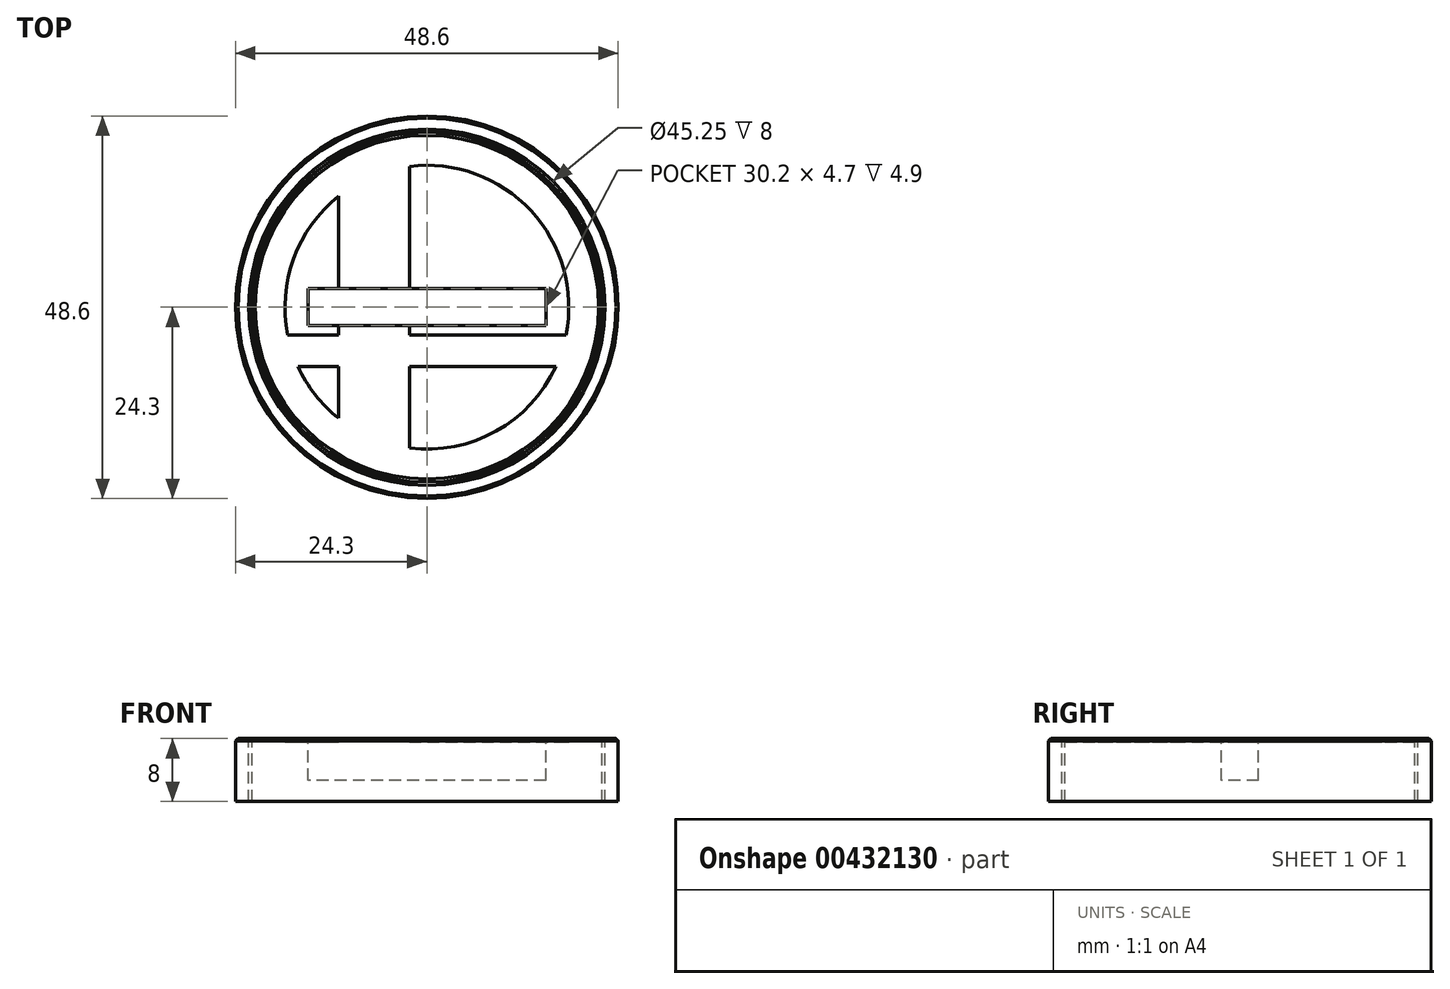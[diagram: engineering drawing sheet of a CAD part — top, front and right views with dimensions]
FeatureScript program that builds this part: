
annotation { "Feature Type Name" : "Feature", "Feature Type Description" : "" }
export const myFeature = defineFeature(function(context is Context, id is Id, definition is map)
    precondition{}
    {
        {
            var Q0;
            Q0=qCreatedBy(makeId("Top.planeOp"),FACE);
            var sketch = newSketch(context, id + "F0", { "sketchPlane" : qUnion([Q0])});
            skCircle(sketch, "E0", {"center": v(0, 0) * mm, "radius": 22.23 * mm});
            skArc(sketch, "E1", {"start": v(-11.22, 14.1) * mm, "mid": v(-16.93, 6.2) * mm, "end": v(-17.68, -3.53) * mm});
            skLineSegment(sketch, "E2", {"start": v(-17.68, -3.53) * mm, "end": v(-11.23, -3.53) * mm});
            skPoint(sketch, "E3", {"position": v(0, -18.02) * mm});
            skLineSegment(sketch, "E4", {"start": v(-16.38, -7.53) * mm, "end": v(-11.23, -7.53) * mm});
            skLineSegment(sketch, "E5", {"start": v(-2.23, 17.89) * mm, "end": v(-2.23, -3.53) * mm});
            skPoint(sketch, "E6", {"position": v(-22.23, 0) * mm});
            skLineSegment(sketch, "E7", {"start": v(-11.23, 14.1) * mm, "end": v(-11.23, -3.52) * mm});
            skLineSegment(sketch, "E8.trimOffspring", {"start": v(-2.23, -3.53) * mm, "end": v(17.68, -3.53) * mm});
            skLineSegment(sketch, "E9.trimOffspring", {"start": v(-2.23, -7.53) * mm, "end": v(16.38, -7.53) * mm});
            skLineSegment(sketch, "E10.trimOffspring", {"start": v(-11.23, -7.52) * mm, "end": v(-11.23, -14.1) * mm});
            skLineSegment(sketch, "E11.trimOffspring", {"start": v(-2.23, -7.53) * mm, "end": v(-2.23, -17.89) * mm});
            skArc(sketch, "E12.trimOffspring", {"start": v(-16.38, -7.53) * mm, "mid": v(-14.19, -11.12) * mm, "end": v(-11.22, -14.1) * mm});
            skArc(sketch, "E13.trimOffspring", {"start": v(-2.23, -17.89) * mm, "mid": v(8.77, -15.75) * mm, "end": v(16.38, -7.53) * mm});
            skArc(sketch, "E14.trimOffspring", {"start": v(17.68, -3.52) * mm, "mid": v(13.2, 12.27) * mm, "end": v(-2.23, 17.89) * mm});
            skSolve(sketch);
        }
        {
            var Q0;
            Q0=makeQuery(id+"F0.imprint","IMPRINT",FACE,{"disambiguationData":[TD([[makeQuery(id+"F0.imprint","IMPRINT",EDGE,{"derivedFrom":sQuery(id+"F0.wireOp",EDGE,"E0")}),1.0]])]});
            var Q1;
            Q1=makeQuery(id+"F0.imprint","IMPRINT",FACE,{"disambiguationData":[TD([[makeQuery(id+"F0.imprint","IMPRINT",EDGE,{"derivedFrom":sQuery(id+"F0.wireOp",EDGE,"E4")}),-1.0]])]});
            var Q2;
            Q2=makeQuery(id+"F0.imprint","IMPRINT",FACE,{"disambiguationData":[TD([[makeQuery(id+"F0.imprint","IMPRINT",EDGE,{"derivedFrom":sQuery(id+"F0.wireOp",EDGE,"E1")}),1.0]])]});
            var Q3;
            Q3=makeQuery(id+"F0.imprint","IMPRINT",FACE,{"disambiguationData":[TD([[makeQuery(id+"F0.imprint","IMPRINT",EDGE,{"derivedFrom":sQuery(id+"F0.wireOp",EDGE,"E5")}),1.0]])]});
            var Q4;
            Q4=makeQuery(id+"F0.imprint","IMPRINT",FACE,{"disambiguationData":[TD([[makeQuery(id+"F0.imprint","IMPRINT",EDGE,{"derivedFrom":sQuery(id+"F0.wireOp",EDGE,"E9.trimOffspring")}),-1.0]])]});
            extrude(context, id + "F1", {"entities" : qUnion([Q0, Q1, Q2, Q3, Q4]), "oppositeDirection" : true, "depth" : 8 * mm});
        }
        {
            var Q0;
            Q0=makeQuery(id+"F0.imprint","IMPRINT",FACE,{"disambiguationData":[TD([[makeQuery(id+"F0.imprint","IMPRINT",EDGE,{"derivedFrom":sQuery(id+"F0.wireOp",EDGE,"E1")}),1.0]])]});
            var Q1;
            Q1=makeQuery(id+"F0.imprint","IMPRINT",FACE,{"disambiguationData":[TD([[makeQuery(id+"F0.imprint","IMPRINT",EDGE,{"derivedFrom":sQuery(id+"F0.wireOp",EDGE,"E5")}),1.0]])]});
            var Q2;
            Q2=makeQuery(id+"F0.imprint","IMPRINT",FACE,{"disambiguationData":[TD([[makeQuery(id+"F0.imprint","IMPRINT",EDGE,{"derivedFrom":sQuery(id+"F0.wireOp",EDGE,"E9.trimOffspring")}),-1.0]])]});
            var Q3;
            Q3=makeQuery(id+"F0.imprint","IMPRINT",FACE,{"disambiguationData":[TD([[makeQuery(id+"F0.imprint","IMPRINT",EDGE,{"derivedFrom":sQuery(id+"F0.wireOp",EDGE,"E4")}),-1.0]])]});
            extrude(context, id + "F2", {"entities" : qUnion([Q0, Q1, Q2, Q3]), "operationType" : NewBodyOperationType.REMOVE, "oppositeDirection" : true, "depth" : 0.4 * mm});
        }
        {
            var Q0;
            Q0=qCreatedBy(makeId("Top.planeOp"),FACE);
            var sketch = newSketch(context, id + "F3", { "sketchPlane" : qUnion([Q0])});
            skLineSegment(sketch, "E15.bottom", {"start": v(15.1, 2.35) * mm, "end": v(-15.1, 2.35) * mm});
            skLineSegment(sketch, "E15.top", {"start": v(15.1, -2.35) * mm, "end": v(-15.1, -2.35) * mm});
            skLineSegment(sketch, "E15.left", {"start": v(15.1, 2.35) * mm, "end": v(15.1, -2.35) * mm});
            skLineSegment(sketch, "E15.right", {"start": v(-15.1, 2.35) * mm, "end": v(-15.1, -2.35) * mm});
            skPoint(sketch, "E15.middle", {"position": v(0, 0) * mm});
            skSolve(sketch);
        }
        {
            var Q0;
            Q0=makeQuery(id+"F3.imprint","IMPRINT",FACE,{"disambiguationData":[TD([[makeQuery(id+"F3.imprint","IMPRINT",EDGE,{"derivedFrom":sQuery(id+"F3.wireOp",EDGE,"E15.bottom")}),1.0]])]});
            extrude(context, id + "F4", {"entities" : qUnion([Q0]), "operationType" : NewBodyOperationType.REMOVE, "oppositeDirection" : true, "depth" : 5.3 * mm});
        }
        {
            var Q0;
            {var subQ0=sQuery(id+"F0.wireOp",EDGE,"E7");Q0=makeQuery(id+"F4.boolean.opBoolean","SPLIT",EDGE,{"disambiguationData":[TD([makeQuery(id+"F2.boolean.opBoolean","COPY",FACE,{"derivedFrom":makeQuery(id+"F2.opExtrude","SWEPT_FACE",FACE,{"disambiguationData":[OSD([sQuery(id+"F0.wireOp",EDGE,"E1")])]})})])],"derivedFrom":makeQuery(id+"F2.boolean.opBoolean","COPY",EDGE,{"derivedFrom":makeQuery(id+"F2.opExtrude","CAP_EDGE",EDGE,{"disambiguationData":[OSD([subQ0])],"isStart":true})})});}
            var Q1;
            Q1=makeQuery(id+"F2.boolean.opBoolean","COPY",EDGE,{"derivedFrom":makeQuery(id+"F2.opExtrude","CAP_EDGE",EDGE,{"disambiguationData":[OSD([sQuery(id+"F0.wireOp",EDGE,"E1")])],"isStart":true})});
            var Q2;
            Q2=makeQuery(id+"F2.boolean.opBoolean","COPY",EDGE,{"derivedFrom":makeQuery(id+"F2.opExtrude","CAP_EDGE",EDGE,{"disambiguationData":[OSD([sQuery(id+"F0.wireOp",EDGE,"E2")])],"isStart":true})});
            var Q3;
            {var subQ0=sQuery(id+"F0.wireOp",EDGE,"E7");Q3=makeQuery(id+"F4.boolean.opBoolean","SPLIT",EDGE,{"disambiguationData":[TD([makeQuery(id+"F2.boolean.opBoolean","COPY",FACE,{"derivedFrom":makeQuery(id+"F2.opExtrude","SWEPT_FACE",FACE,{"disambiguationData":[OSD([sQuery(id+"F0.wireOp",EDGE,"E2")])]})})])],"derivedFrom":makeQuery(id+"F2.boolean.opBoolean","COPY",EDGE,{"derivedFrom":makeQuery(id+"F2.opExtrude","CAP_EDGE",EDGE,{"disambiguationData":[OSD([subQ0])],"isStart":true})})});}
            var Q4;
            Q4=makeQuery(id+"F2.boolean.opBoolean","COPY",EDGE,{"derivedFrom":makeQuery(id+"F2.opExtrude","CAP_EDGE",EDGE,{"disambiguationData":[OSD([sQuery(id+"F0.wireOp",EDGE,"E14.trimOffspring")])],"isStart":true})});
            var Q5;
            {var subQ0=sQuery(id+"F0.wireOp",EDGE,"E5");Q5=makeQuery(id+"F4.boolean.opBoolean","SPLIT",EDGE,{"disambiguationData":[TD([makeQuery(id+"F2.boolean.opBoolean","COPY",FACE,{"derivedFrom":makeQuery(id+"F2.opExtrude","SWEPT_FACE",FACE,{"disambiguationData":[OSD([sQuery(id+"F0.wireOp",EDGE,"E14.trimOffspring")])]})})])],"derivedFrom":makeQuery(id+"F2.boolean.opBoolean","COPY",EDGE,{"derivedFrom":makeQuery(id+"F2.opExtrude","CAP_EDGE",EDGE,{"disambiguationData":[OSD([subQ0])],"isStart":true})})});}
            var Q6;
            Q6=makeQuery(id+"F2.boolean.opBoolean","COPY",EDGE,{"derivedFrom":makeQuery(id+"F2.opExtrude","CAP_EDGE",EDGE,{"disambiguationData":[OSD([sQuery(id+"F0.wireOp",EDGE,"E8.trimOffspring")])],"isStart":true})});
            var Q7;
            Q7=makeQuery(id+"F2.boolean.opBoolean","COPY",EDGE,{"derivedFrom":makeQuery(id+"F2.opExtrude","CAP_EDGE",EDGE,{"disambiguationData":[OSD([sQuery(id+"F0.wireOp",EDGE,"E9.trimOffspring")])],"isStart":true})});
            var Q8;
            Q8=makeQuery(id+"F2.boolean.opBoolean","COPY",EDGE,{"derivedFrom":makeQuery(id+"F2.opExtrude","CAP_EDGE",EDGE,{"disambiguationData":[OSD([sQuery(id+"F0.wireOp",EDGE,"E13.trimOffspring")])],"isStart":true})});
            var Q9;
            {var subQ0=sQuery(id+"F0.wireOp",EDGE,"E5");Q9=makeQuery(id+"F4.boolean.opBoolean","SPLIT",EDGE,{"disambiguationData":[TD([makeQuery(id+"F2.boolean.opBoolean","COPY",FACE,{"derivedFrom":makeQuery(id+"F2.opExtrude","SWEPT_FACE",FACE,{"disambiguationData":[OSD([sQuery(id+"F0.wireOp",EDGE,"E8.trimOffspring")])]})})])],"derivedFrom":makeQuery(id+"F2.boolean.opBoolean","COPY",EDGE,{"derivedFrom":makeQuery(id+"F2.opExtrude","CAP_EDGE",EDGE,{"disambiguationData":[OSD([subQ0])],"isStart":true})})});}
            var Q10;
            Q10=makeQuery(id+"F2.boolean.opBoolean","COPY",EDGE,{"derivedFrom":makeQuery(id+"F2.opExtrude","CAP_EDGE",EDGE,{"disambiguationData":[OSD([sQuery(id+"F0.wireOp",EDGE,"E11.trimOffspring")])],"isStart":true})});
            var Q11;
            Q11=makeQuery(id+"F2.boolean.opBoolean","COPY",EDGE,{"derivedFrom":makeQuery(id+"F2.opExtrude","CAP_EDGE",EDGE,{"disambiguationData":[OSD([sQuery(id+"F0.wireOp",EDGE,"E4")])],"isStart":true})});
            var Q12;
            Q12=makeQuery(id+"F2.boolean.opBoolean","COPY",EDGE,{"derivedFrom":makeQuery(id+"F2.opExtrude","CAP_EDGE",EDGE,{"disambiguationData":[OSD([sQuery(id+"F0.wireOp",EDGE,"E12.trimOffspring")])],"isStart":true})});
            var Q13;
            Q13=makeQuery(id+"F2.boolean.opBoolean","COPY",EDGE,{"derivedFrom":makeQuery(id+"F2.opExtrude","CAP_EDGE",EDGE,{"disambiguationData":[OSD([sQuery(id+"F0.wireOp",EDGE,"E10.trimOffspring")])],"isStart":true})});
            var Q14;
            Q14=makeQuery(id+"F4.boolean.opBoolean","COPY",EDGE,{"derivedFrom":makeQuery(id+"F4.opExtrude","CAP_EDGE",EDGE,{"disambiguationData":[OSD([sQuery(id+"F3.wireOp",EDGE,"E15.bottom")])],"isStart":true})});
            var Q15;
            Q15=makeQuery(id+"F4.boolean.opBoolean","COPY",EDGE,{"derivedFrom":makeQuery(id+"F4.opExtrude","CAP_EDGE",EDGE,{"disambiguationData":[OSD([sQuery(id+"F3.wireOp",EDGE,"E15.top")])],"isStart":true})});
            var Q16;
            Q16=makeQuery(id+"F1.opExtrude","CAP_EDGE",EDGE,{"disambiguationData":[OSD([sQuery(id+"F0.wireOp",EDGE,"E0")])],"isStart":true});
            chamfer(context, id + "F5", {"entities" : qUnion([Q0, Q1, Q2, Q3, Q4, Q5, Q6, Q7, Q8, Q9, Q10, Q11, Q12, Q13, Q14, Q15, Q16]), "width" : 0.4 * mm, "tangentPropagation" : true});
        }
        {
            var Q0;
            Q0=qCreatedBy(makeId("Top.planeOp"),FACE);
            var sketch = newSketch(context, id + "F6", { "sketchPlane" : qUnion([Q0])});
            skCircle(sketch, "E16", {"center": v(0, 0) * mm, "radius": 24.3 * mm});
            skCircle(sketch, "E17", {"center": v(0, 0) * mm, "radius": 22.63 * mm});
            skSolve(sketch);
        }
        {
            var Q0;
            Q0=makeQuery(id+"F6.imprint","IMPRINT",FACE,{"disambiguationData":[TD([[makeQuery(id+"F6.imprint","IMPRINT",EDGE,{"derivedFrom":sQuery(id+"F6.wireOp",EDGE,"E16")}),1.0]])]});
            var Q1;
            Q1=makeQuery(id+"F1.opExtrude","CAP_FACE",FACE,{"disambiguationData":[OSD([sQuery(id+"F0.wireOp",EDGE,"E0")])],"isStart":false});
            extrude(context, id + "F7", {"entities" : qUnion([Q0]), "endBound" : BoundingType.UP_TO_SURFACE, "oppositeDirection" : true, "endBoundEntityFace" : qUnion([Q1]), "depth" : 25 * mm});
        }
        {
            var Q0;
            Q0=makeQuery(id+"F7.opExtrude","CAP_EDGE",EDGE,{"disambiguationData":[OSD([sQuery(id+"F6.wireOp",EDGE,"E16")])],"isStart":true});
            chamfer(context, id + "F8", {"entities" : qUnion([Q0]), "width" : 0.3 * mm, "tangentPropagation" : true});
        }
    });
